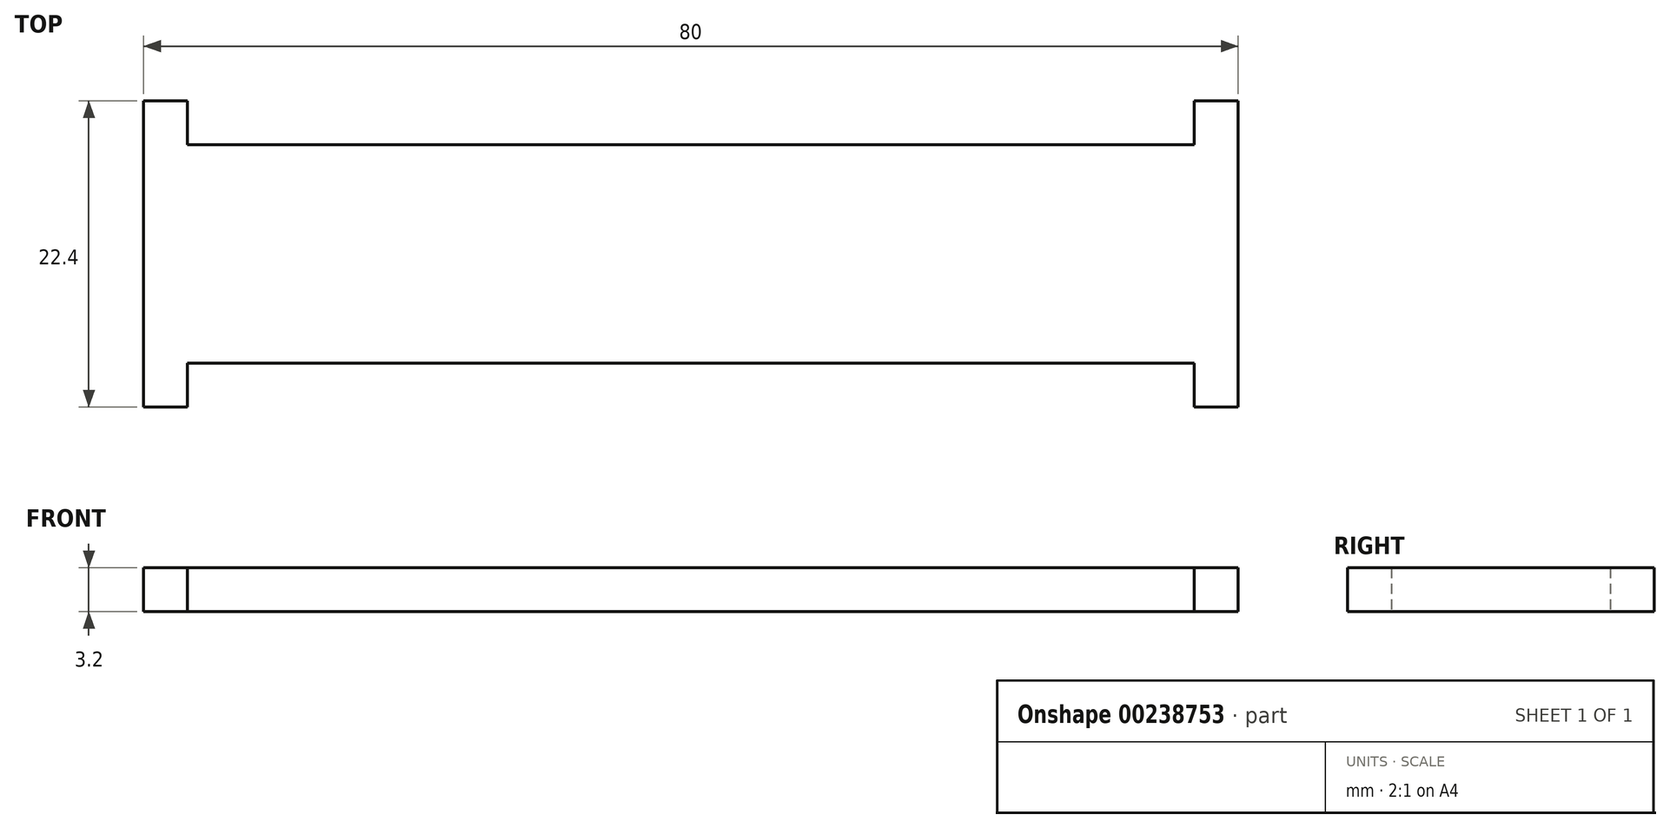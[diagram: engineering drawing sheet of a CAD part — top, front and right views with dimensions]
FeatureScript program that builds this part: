
annotation { "Feature Type Name" : "Feature", "Feature Type Description" : "" }
export const myFeature = defineFeature(function(context is Context, id is Id, definition is map)
    precondition{}
    {
        {
            var Q0;
            Q0=qCreatedBy(makeId("Top.planeOp"),FACE);
            var sketch = newSketch(context, id + "F0", { "sketchPlane" : qUnion([Q0])});
            skLineSegment(sketch, "E0.bottom", {"start": v(36.8, 8) * mm, "end": v(-36.8, 8) * mm});
            skLineSegment(sketch, "E0.top", {"start": v(36.8, -8) * mm, "end": v(-36.8, -8) * mm});
            skLineSegment(sketch, "E0.left", {"start": v(40, 8) * mm, "end": v(40, -8) * mm});
            skLineSegment(sketch, "E0.right", {"start": v(-40, 8) * mm, "end": v(-40, -8) * mm});
            skPoint(sketch, "E0.middle", {"position": v(0, 0) * mm});
            skLineSegment(sketch, "E1.top", {"start": v(-40, 11.2) * mm, "end": v(-36.8, 11.2) * mm});
            skLineSegment(sketch, "E1.left", {"start": v(-40, 8) * mm, "end": v(-40, 11.2) * mm});
            skLineSegment(sketch, "E1.right", {"start": v(-36.8, 8) * mm, "end": v(-36.8, 11.2) * mm});
            skLineSegment(sketch, "E2.MirrorCS", {"start": v(40, 11.2) * mm, "end": v(36.8, 11.2) * mm});
            skLineSegment(sketch, "E3.MirrorCS", {"start": v(36.8, 8) * mm, "end": v(36.8, 11.2) * mm});
            skLineSegment(sketch, "E4.MirrorCS", {"start": v(40, 8) * mm, "end": v(40, 11.2) * mm});
            skLineSegment(sketch, "E5.MirrorCS", {"start": v(-40, -11.2) * mm, "end": v(-36.8, -11.2) * mm});
            skLineSegment(sketch, "E6.MirrorCS", {"start": v(40, -11.2) * mm, "end": v(36.8, -11.2) * mm});
            skLineSegment(sketch, "E7.MirrorCS", {"start": v(-40, -8) * mm, "end": v(-40, -11.2) * mm});
            skLineSegment(sketch, "E8.MirrorCS", {"start": v(-36.8, -8) * mm, "end": v(-36.8, -11.2) * mm});
            skLineSegment(sketch, "E9.MirrorCS", {"start": v(40, -8) * mm, "end": v(40, -11.2) * mm});
            skLineSegment(sketch, "E10.MirrorCS", {"start": v(36.8, -8) * mm, "end": v(36.8, -11.2) * mm});
            skSolve(sketch);
        }
        {
            var Q0;
            Q0 = qSketchRegion(id + "F0", true);
            extrude(context, id + "F1", {"entities" : qUnion([Q0]), "depth" : 3.2 * mm});
        }
    });
